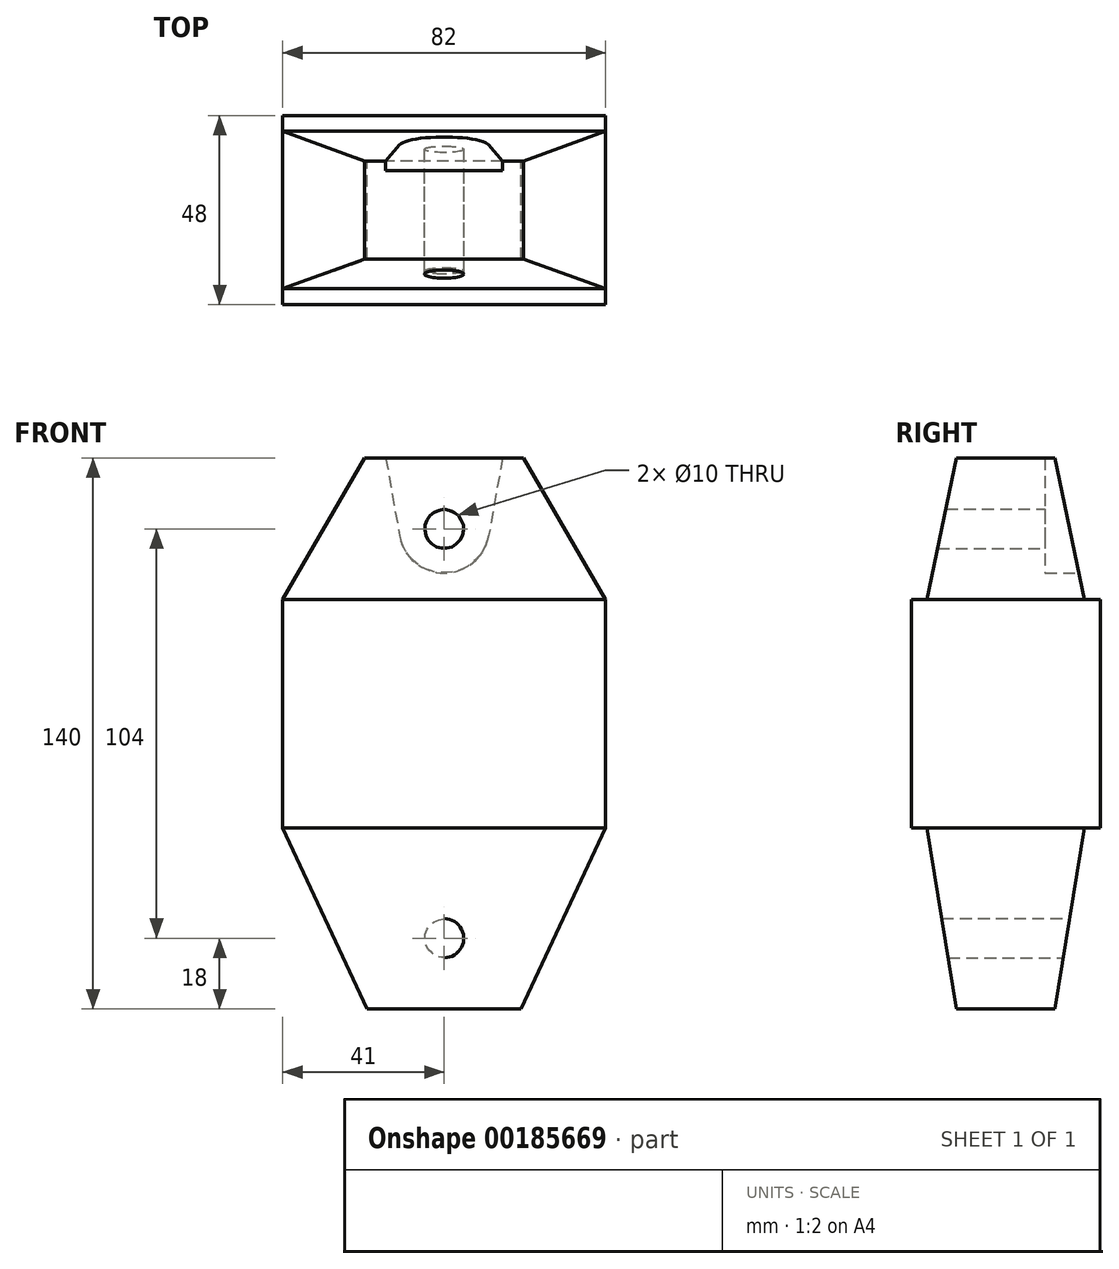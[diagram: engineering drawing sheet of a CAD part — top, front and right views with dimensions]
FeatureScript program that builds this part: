
annotation { "Feature Type Name" : "Feature", "Feature Type Description" : "" }
export const myFeature = defineFeature(function(context is Context, id is Id, definition is map)
    precondition{}
    {
        {
            var Q0;
            Q0=qCreatedBy(makeId("Right.planeOp"),FACE);
            var sketch = newSketch(context, id + "F0", { "sketchPlane" : qUnion([Q0])});
            skLineSegment(sketch, "E0.bottom", {"start": v(-12.5, 65) * mm, "end": v(12.5, 65) * mm});
            skLineSegment(sketch, "E1", {"start": v(-24, 29) * mm, "end": v(-20, 29) * mm});
            skLineSegment(sketch, "E2", {"start": v(-12.5, 65) * mm, "end": v(-20, 29) * mm});
            skLineSegment(sketch, "E3.MirrorCS", {"start": v(24, 29) * mm, "end": v(20, 29) * mm});
            skLineSegment(sketch, "E4.MirrorCS", {"start": v(24, 29) * mm, "end": v(24, -29) * mm});
            skLineSegment(sketch, "E5.MirrorCS", {"start": v(12.5, 65) * mm, "end": v(20, 29) * mm});
            skLineSegment(sketch, "E6.MirrorCS", {"start": v(-24, -29) * mm, "end": v(-20, -29) * mm});
            skLineSegment(sketch, "E7.MirrorCS", {"start": v(24, -29) * mm, "end": v(20, -29) * mm});
            skLineSegment(sketch, "E8.MirrorCS", {"start": v(-24, -29) * mm, "end": v(-24, 29) * mm});
            skLineSegment(sketch, "E9.MirrorCS", {"start": v(12.5, -75) * mm, "end": v(-12.5, -75) * mm});
            skPoint(sketch, "E10.orphan", {"position": v(0, 65) * mm});
            skLineSegment(sketch, "E11", {"start": v(20, -29) * mm, "end": v(12.5, -75) * mm});
            skLineSegment(sketch, "E12", {"start": v(-12.5, -75) * mm, "end": v(-20, -29) * mm});
            skSolve(sketch);
        }
        {
            var Q0;
            Q0=makeQuery(id+"F0.imprint","IMPRINT",FACE,{"disambiguationData":[TD([[makeQuery(id+"F0.imprint","IMPRINT",EDGE,{"derivedFrom":sQuery(id+"F0.wireOp",EDGE,"E0.bottom")}),-1.0]])]});
            extrude(context, id + "F1", {"entities" : qUnion([Q0]), "depth" : 82 * mm});
        }
        {
            var Q0;
            Q0=makeQuery(id+"F1.opExtrude","SWEPT_FACE",FACE,{"disambiguationData":[OSD([sQuery(id+"F0.wireOp",EDGE,"E4.MirrorCS")])]});
            var sketch = newSketch(context, id + "F2", { "sketchPlane" : qUnion([Q0])});
            skLineSegment(sketch, "E13", {"start": v(-55.44, 75) * mm, "end": v(-92, 11.68) * mm});
            skLineSegment(sketch, "E14", {"start": v(-92, 11.68) * mm, "end": v(-92, -7.55) * mm});
            skLineSegment(sketch, "E15", {"start": v(-92, -7.55) * mm, "end": v(-55.89, -85) * mm});
            skLineSegment(sketch, "E16", {"start": v(-55.89, -85) * mm, "end": v(-26.11, -85) * mm});
            skLineSegment(sketch, "E17", {"start": v(10, -7.55) * mm, "end": v(-26.11, -85) * mm});
            skLineSegment(sketch, "E18", {"start": v(10, -7.55) * mm, "end": v(10, 11.68) * mm});
            skLineSegment(sketch, "E19", {"start": v(10, 11.68) * mm, "end": v(-26.56, 75) * mm});
            skLineSegment(sketch, "E20", {"start": v(-26.56, 75) * mm, "end": v(-55.44, 75) * mm});
            skCircle(sketch, "E21", {"center": v(-41, 47) * mm, "radius": 5 * mm});
            skCircle(sketch, "E22", {"center": v(-41, -57) * mm, "radius": 5 * mm});
            skSolve(sketch);
        }
        {
            var Q0;
            Q0 = qSketchRegion(id + "F2", true);
            extrude(context, id + "F3", {"entities" : qUnion([Q0]), "operationType" : NewBodyOperationType.INTERSECT, "endBound" : BoundingType.UP_TO_NEXT, "oppositeDirection" : true, "depth" : 25 * mm});
        }
        {
            var Q0;
            Q0=makeQuery(id+"F1.opExtrude","SWEPT_FACE",FACE,{"disambiguationData":[OSD([sQuery(id+"F0.wireOp",EDGE,"E4.MirrorCS")])]});
            var sketch = newSketch(context, id + "F4", { "sketchPlane" : qUnion([Q0])});
            skLineSegment(sketch, "E23", {"start": v(-41, 35.8) * mm, "end": v(-41, 66) * mm});
            skPoint(sketch, "E23.startSnap0", {"position": v(-41, 29) * mm});
            skLineSegment(sketch, "E24", {"start": v(-41, 66) * mm, "end": v(-26, 66) * mm});
            skArc(sketch, "E25", {"start": v(-41, 35.8) * mm, "mid": v(-33.61, 38.48) * mm, "end": v(-29.68, 45.29) * mm});
            skLineSegment(sketch, "E26", {"start": v(-26, 66) * mm, "end": v(-29.68, 45.29) * mm});
            skLineSegment(sketch, "E27.MirrorCS", {"start": v(-41, 66) * mm, "end": v(-56, 66) * mm});
            skLineSegment(sketch, "E28.MirrorCS", {"start": v(-56, 66) * mm, "end": v(-52.32, 45.29) * mm});
            skArc(sketch, "E29.MirrorCS", {"start": v(-41, 35.8) * mm, "mid": v(-48.39, 38.48) * mm, "end": v(-52.32, 45.29) * mm});
            skSolve(sketch);
        }
        {
            var Q0;
            Q0 = qSketchRegion(id + "F4", true);
            extrude(context, id + "F5", {"entities" : qUnion([Q0]), "operationType" : NewBodyOperationType.REMOVE, "oppositeDirection" : true, "depth" : 14 * mm});
        }
    });
